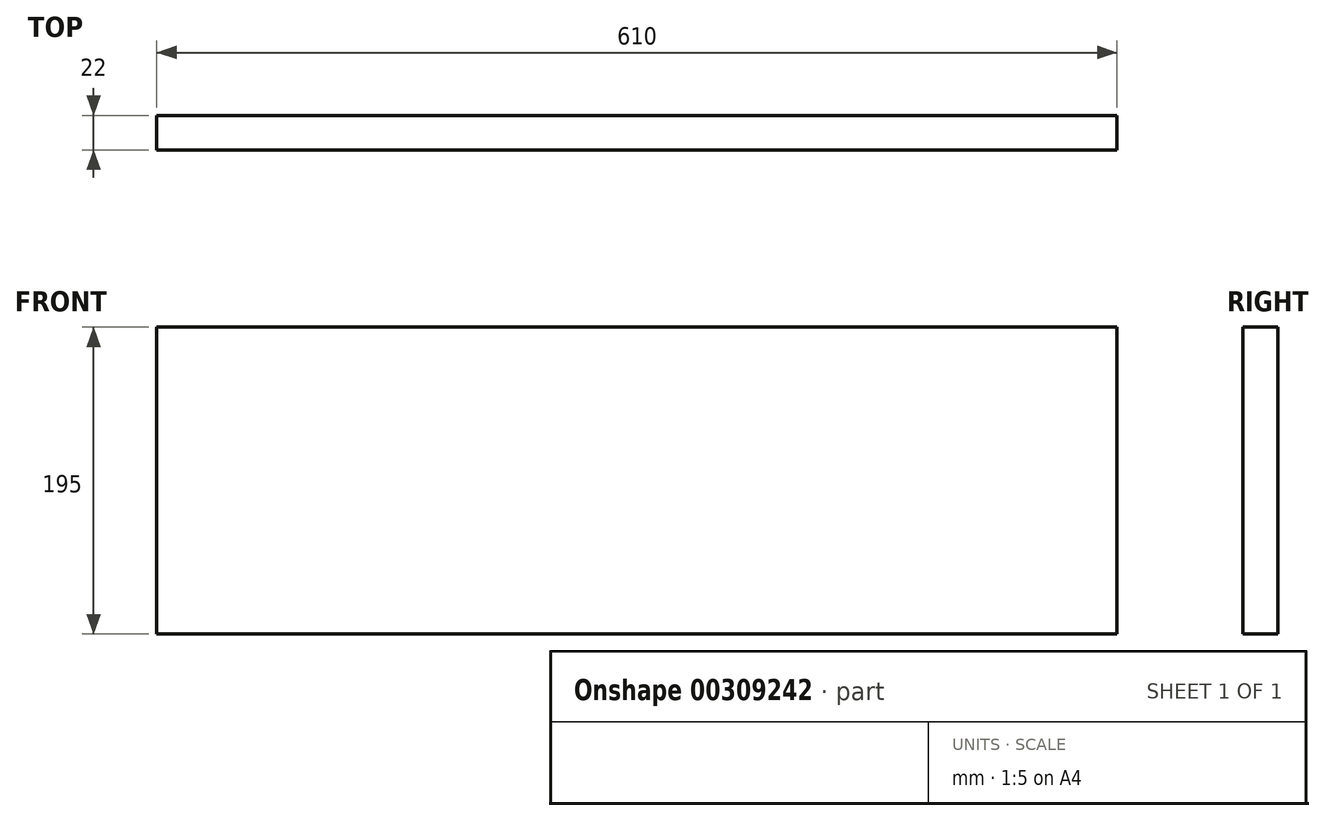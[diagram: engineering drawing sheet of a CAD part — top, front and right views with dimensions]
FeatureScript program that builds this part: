
annotation { "Feature Type Name" : "Feature", "Feature Type Description" : "" }
export const myFeature = defineFeature(function(context is Context, id is Id, definition is map)
    precondition{}
    {
        {
            var Q0;
            Q0=qCreatedBy(makeId("Right.planeOp"),FACE);
            var sketch = newSketch(context, id + "F0", { "sketchPlane" : qUnion([Q0])});
            skLineSegment(sketch, "E0.bottom", {"start": v(0, 0) * mm, "end": v(22, 0) * mm});
            skLineSegment(sketch, "E0.top", {"start": v(0, 195) * mm, "end": v(22, 195) * mm});
            skLineSegment(sketch, "E0.left", {"start": v(0, 0) * mm, "end": v(0, 195) * mm});
            skLineSegment(sketch, "E0.right", {"start": v(22, 0) * mm, "end": v(22, 195) * mm});
            skSolve(sketch);
        }
        {
            var Q0;
            Q0=makeQuery(id+"F0.imprint","IMPRINT",FACE,{"disambiguationData":[TD([[makeQuery(id+"F0.imprint","IMPRINT",EDGE,{"derivedFrom":sQuery(id+"F0.wireOp",EDGE,"E0.bottom")}),1.0]])]});
            extrude(context, id + "F1", {"entities" : qUnion([Q0]), "depth" : 610 * mm});
        }
    });
